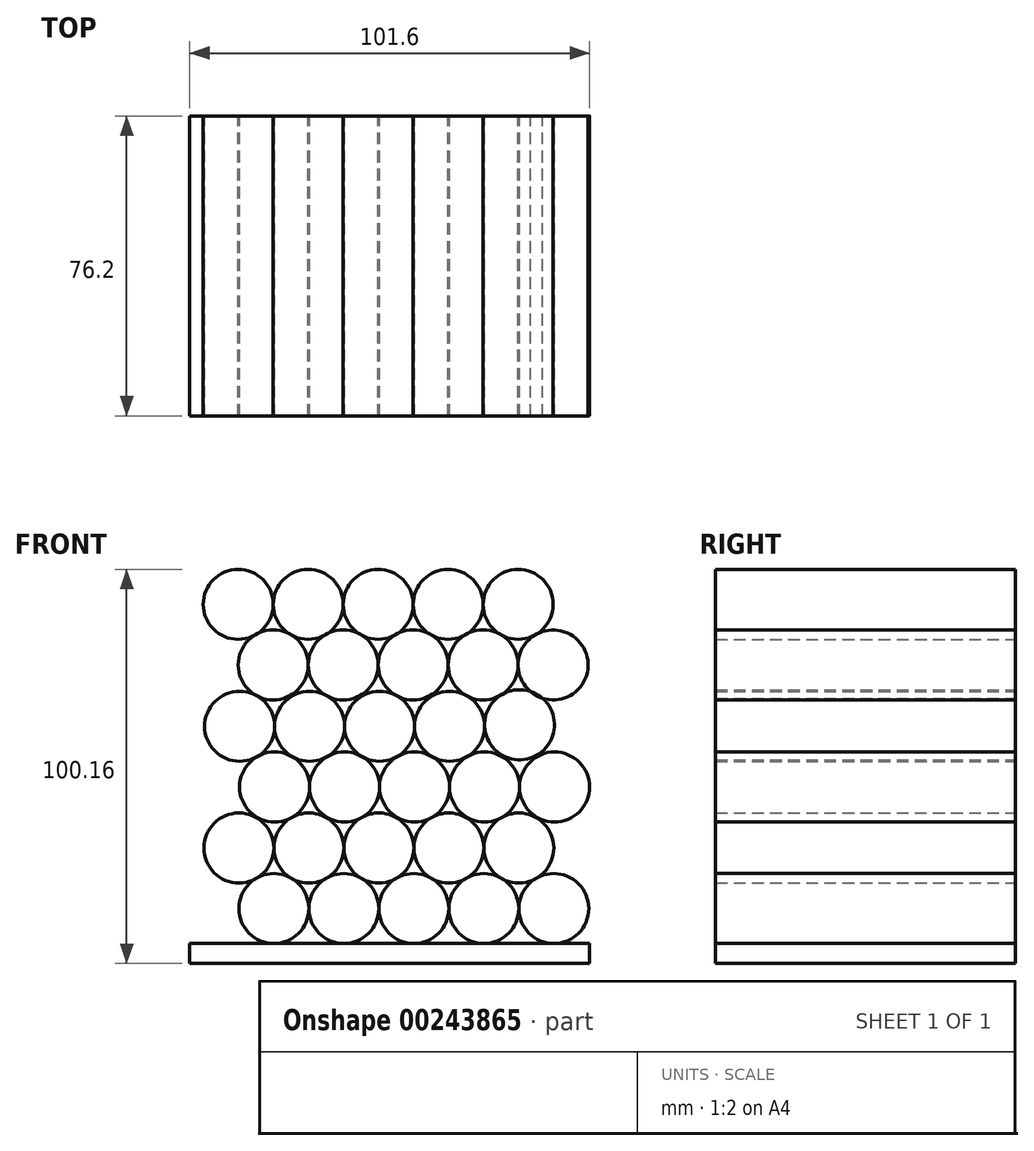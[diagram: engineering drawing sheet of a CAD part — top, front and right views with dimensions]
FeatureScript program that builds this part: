
annotation { "Feature Type Name" : "Feature", "Feature Type Description" : "" }
export const myFeature = defineFeature(function(context is Context, id is Id, definition is map)
    precondition{}
    {
        {
            var Q0;
            Q0=qCreatedBy(makeId("Front.planeOp"),FACE);
            var sketch = newSketch(context, id + "F0", { "sketchPlane" : qUnion([Q0])});
            skCircle(sketch, "E0", {"center": v(-29.45, -16.57) * mm, "radius": 8.9 * mm});
            skCircle(sketch, "E1", {"center": v(-11.67, -16.57) * mm, "radius": 8.9 * mm});
            skCircle(sketch, "E2", {"center": v(6.11, -16.57) * mm, "radius": 8.9 * mm});
            skCircle(sketch, "E3", {"center": v(23.9, -16.57) * mm, "radius": 8.9 * mm});
            skCircle(sketch, "E4", {"center": v(41.67, -16.57) * mm, "radius": 8.9 * mm});
            skLineSegment(sketch, "E5.bottom", {"start": v(-50.8, -25.46) * mm, "end": v(50.8, -25.46) * mm});
            skLineSegment(sketch, "E5.top", {"start": v(-50.8, -30.54) * mm, "end": v(50.8, -30.54) * mm});
            skLineSegment(sketch, "E5.left", {"start": v(-50.8, -25.46) * mm, "end": v(-50.8, -30.54) * mm});
            skLineSegment(sketch, "E5.right", {"start": v(50.8, -25.46) * mm, "end": v(50.8, -30.54) * mm});
            skCircle(sketch, "E6", {"center": v(-38.34, -1.17) * mm, "radius": 8.9 * mm});
            skCircle(sketch, "E7", {"center": v(-20.56, -1.17) * mm, "radius": 8.9 * mm});
            skCircle(sketch, "E8", {"center": v(-2.78, -1.17) * mm, "radius": 8.9 * mm});
            skCircle(sketch, "E9", {"center": v(15, -1.17) * mm, "radius": 8.9 * mm});
            skCircle(sketch, "E10", {"center": v(32.78, -1.17) * mm, "radius": 8.9 * mm});
            skCircle(sketch, "E11", {"center": v(-29.26, 14.34) * mm, "radius": 8.9 * mm});
            skCircle(sketch, "E12", {"center": v(-11.48, 14.34) * mm, "radius": 8.9 * mm});
            skCircle(sketch, "E13", {"center": v(6.3, 14.34) * mm, "radius": 8.9 * mm});
            skCircle(sketch, "E14", {"center": v(24.08, 14.34) * mm, "radius": 8.9 * mm});
            skCircle(sketch, "E15", {"center": v(41.86, 14.34) * mm, "radius": 8.9 * mm});
            skCircle(sketch, "E16", {"center": v(-38.15, 29.73) * mm, "radius": 8.9 * mm});
            skCircle(sketch, "E17", {"center": v(-20.37, 29.73) * mm, "radius": 8.9 * mm});
            skCircle(sketch, "E18", {"center": v(-2.6, 29.73) * mm, "radius": 8.9 * mm});
            skCircle(sketch, "E19", {"center": v(15.19, 29.73) * mm, "radius": 8.9 * mm});
            skCircle(sketch, "E20", {"center": v(32.96, 30.14) * mm, "radius": 8.9 * mm});
            skCircle(sketch, "E21", {"center": v(-29.62, 45.33) * mm, "radius": 8.9 * mm});
            skCircle(sketch, "E22", {"center": v(-11.84, 45.33) * mm, "radius": 8.9 * mm});
            skCircle(sketch, "E23", {"center": v(5.94, 45.33) * mm, "radius": 8.9 * mm});
            skCircle(sketch, "E24", {"center": v(23.72, 45.33) * mm, "radius": 8.9 * mm});
            skCircle(sketch, "E25", {"center": v(41.5, 45.33) * mm, "radius": 8.9 * mm});
            skCircle(sketch, "E26", {"center": v(-38.51, 60.73) * mm, "radius": 8.9 * mm});
            skCircle(sketch, "E27", {"center": v(-20.73, 60.73) * mm, "radius": 8.9 * mm});
            skCircle(sketch, "E28", {"center": v(-2.95, 60.73) * mm, "radius": 8.9 * mm});
            skCircle(sketch, "E29", {"center": v(14.83, 60.73) * mm, "radius": 8.9 * mm});
            skCircle(sketch, "E30", {"center": v(32.6, 60.73) * mm, "radius": 8.9 * mm});
            skSolve(sketch);
        }
        {
            var Q0;
            {var subQ0=sQuery(id+"F0.wireOp",EDGE,"0c1801c8-23d2-4a07-8585-4b4ae403161c");var subQ1=makeQuery(id+"F0.imprint","INTERSECT",VERTEX,{"derivedFrom":[sQuery(id+"F0.wireOp",EDGE,"f0896b75-7ff4-490b-9eb5-08945ea8ef80"),subQ0]});Q0=makeQuery(id+"F0.imprint","IMPRINT",FACE,{"disambiguationData":[TD([[makeQuery(id+"F0.imprint","IMPRINT",EDGE,{"disambiguationData":[TD([[subQ1,1.0]])],"derivedFrom":subQ0}),1.0]])]});}
            var Q1;
            {var subQ0=sQuery(id+"F0.wireOp",EDGE,"5af625b9-71d9-4944-9748-d1b5f725a47c");var subQ1=makeQuery(id+"F0.imprint","INTERSECT",VERTEX,{"derivedFrom":[sQuery(id+"F0.wireOp",EDGE,"0c1801c8-23d2-4a07-8585-4b4ae403161c"),subQ0]});Q1=makeQuery(id+"F0.imprint","IMPRINT",FACE,{"disambiguationData":[TD([[makeQuery(id+"F0.imprint","IMPRINT",EDGE,{"disambiguationData":[TD([[subQ1,1.0]])],"derivedFrom":subQ0}),1.0]])]});}
            var Q2;
            {var subQ0=sQuery(id+"F0.wireOp",EDGE,"cf587e86-f61d-495c-ab6c-7963b9340b9b");var subQ1=makeQuery(id+"F0.imprint","INTERSECT",VERTEX,{"derivedFrom":[sQuery(id+"F0.wireOp",EDGE,"5af625b9-71d9-4944-9748-d1b5f725a47c"),subQ0]});Q2=makeQuery(id+"F0.imprint","IMPRINT",FACE,{"disambiguationData":[TD([[makeQuery(id+"F0.imprint","IMPRINT",EDGE,{"disambiguationData":[TD([[subQ1,-1.0]])],"derivedFrom":subQ0}),1.0]])]});}
            var Q3;
            {var subQ0=sQuery(id+"F0.wireOp",EDGE,"6513f72b-f417-4675-a262-e46438cbcac2");var subQ1=makeQuery(id+"F0.imprint","INTERSECT",VERTEX,{"derivedFrom":[subQ0,sQuery(id+"F0.wireOp",EDGE,"cf587e86-f61d-495c-ab6c-7963b9340b9b")]});Q3=makeQuery(id+"F0.imprint","IMPRINT",FACE,{"disambiguationData":[TD([[makeQuery(id+"F0.imprint","IMPRINT",EDGE,{"disambiguationData":[TD([[subQ1,-1.0]])],"derivedFrom":subQ0}),1.0]])]});}
            var Q4;
            {var subQ0=sQuery(id+"F0.wireOp",EDGE,"b3fe10dc-f5bd-422b-85db-0323ad2a796b");var subQ4=makeQuery(id+"F0.imprint","INTERSECT",VERTEX,{"derivedFrom":[subQ0,sQuery(id+"F0.wireOp",EDGE,"cf587e86-f61d-495c-ab6c-7963b9340b9b")]});Q4=makeQuery(id+"F0.imprint","IMPRINT",FACE,{"disambiguationData":[TD([[makeQuery(id+"F0.imprint","IMPRINT",EDGE,{"disambiguationData":[TD([[subQ4,1.0]])],"derivedFrom":subQ0}),1.0]])]});}
            var Q5;
            {var subQ0=sQuery(id+"F0.wireOp",EDGE,"20095c58-7453-4e6b-84d0-4050fc440cec");var subQ4=makeQuery(id+"F0.imprint","INTERSECT",VERTEX,{"derivedFrom":[subQ0,sQuery(id+"F0.wireOp",EDGE,"5af625b9-71d9-4944-9748-d1b5f725a47c")]});Q5=makeQuery(id+"F0.imprint","IMPRINT",FACE,{"disambiguationData":[TD([[makeQuery(id+"F0.imprint","IMPRINT",EDGE,{"disambiguationData":[TD([[subQ4,1.0]])],"derivedFrom":subQ0}),1.0]])]});}
            var Q6;
            {var subQ0=sQuery(id+"F0.wireOp",EDGE,"f0896b75-7ff4-490b-9eb5-08945ea8ef80");var subQ1=makeQuery(id+"F0.imprint","INTERSECT",VERTEX,{"derivedFrom":[subQ0,sQuery(id+"F0.wireOp",EDGE,"0c1801c8-23d2-4a07-8585-4b4ae403161c")]});Q6=makeQuery(id+"F0.imprint","IMPRINT",FACE,{"disambiguationData":[TD([[makeQuery(id+"F0.imprint","IMPRINT",EDGE,{"disambiguationData":[TD([[subQ1,1.0]])],"derivedFrom":subQ0}),1.0]])]});}
            var Q7;
            {var subQ0=sQuery(id+"F0.wireOp",EDGE,"E0");var subQ1=makeQuery(id+"F0.imprint","INTERSECT",VERTEX,{"derivedFrom":[sQuery(id+"F0.wireOp",EDGE,"f0896b75-7ff4-490b-9eb5-08945ea8ef80"),subQ0]});Q7=makeQuery(id+"F0.imprint","IMPRINT",FACE,{"disambiguationData":[TD([[makeQuery(id+"F0.imprint","IMPRINT",EDGE,{"disambiguationData":[TD([[subQ1,1.0]])],"derivedFrom":subQ0}),1.0]])]});}
            var Q8;
            {var subQ0=sQuery(id+"F0.wireOp",EDGE,"E1");var subQ4=makeQuery(id+"F0.imprint","INTERSECT",VERTEX,{"derivedFrom":[sQuery(id+"F0.wireOp",EDGE,"20095c58-7453-4e6b-84d0-4050fc440cec"),subQ0]});Q8=makeQuery(id+"F0.imprint","IMPRINT",FACE,{"disambiguationData":[TD([[makeQuery(id+"F0.imprint","IMPRINT",EDGE,{"disambiguationData":[TD([[subQ4,1.0]])],"derivedFrom":subQ0}),1.0]])]});}
            var Q9;
            {var subQ0=sQuery(id+"F0.wireOp",EDGE,"E2");var subQ4=makeQuery(id+"F0.imprint","INTERSECT",VERTEX,{"derivedFrom":[sQuery(id+"F0.wireOp",EDGE,"b3fe10dc-f5bd-422b-85db-0323ad2a796b"),subQ0]});Q9=makeQuery(id+"F0.imprint","IMPRINT",FACE,{"disambiguationData":[TD([[makeQuery(id+"F0.imprint","IMPRINT",EDGE,{"disambiguationData":[TD([[subQ4,1.0]])],"derivedFrom":subQ0}),1.0]])]});}
            var Q10;
            {var subQ0=sQuery(id+"F0.wireOp",EDGE,"E3");var subQ4=makeQuery(id+"F0.imprint","INTERSECT",VERTEX,{"derivedFrom":[sQuery(id+"F0.wireOp",EDGE,"6513f72b-f417-4675-a262-e46438cbcac2"),subQ0]});Q10=makeQuery(id+"F0.imprint","IMPRINT",FACE,{"disambiguationData":[TD([[makeQuery(id+"F0.imprint","IMPRINT",EDGE,{"disambiguationData":[TD([[subQ4,1.0]])],"derivedFrom":subQ0}),1.0]])]});}
            var Q11;
            {var subQ0=sQuery(id+"F0.wireOp",EDGE,"E4");var subQ1=makeQuery(id+"F0.imprint","INTERSECT",VERTEX,{"derivedFrom":[sQuery(id+"F0.wireOp",EDGE,"6513f72b-f417-4675-a262-e46438cbcac2"),subQ0]});Q11=makeQuery(id+"F0.imprint","IMPRINT",FACE,{"disambiguationData":[TD([[makeQuery(id+"F0.imprint","IMPRINT",EDGE,{"disambiguationData":[TD([[subQ1,-1.0]])],"derivedFrom":subQ0}),1.0]])]});}
            var Q12;
            Q12=makeQuery(id+"F0.imprint","IMPRINT",FACE,{"disambiguationData":[TD([[makeQuery(id+"F0.imprint","IMPRINT",EDGE,{"derivedFrom":sQuery(id+"F0.wireOp",EDGE,"E5.top")}),1.0]])]});
            var Q13;
            {var subQ0=sQuery(id+"F0.wireOp",EDGE,"b7209964-fce2-4c74-a03b-dcfcf9720273");var subQ1=makeQuery(id+"F0.imprint","INTERSECT",VERTEX,{"derivedFrom":[subQ0,sQuery(id+"F0.wireOp",EDGE,"826bc404-7e04-4ebb-a8bb-261f92a73414")]});Q13=makeQuery(id+"F0.imprint","IMPRINT",FACE,{"disambiguationData":[TD([[makeQuery(id+"F0.imprint","IMPRINT",EDGE,{"disambiguationData":[TD([[subQ1,1.0]])],"derivedFrom":subQ0}),1.0]])]});}
            var Q14;
            {var subQ0=sQuery(id+"F0.wireOp",EDGE,"4bfdec23-dac0-4773-80be-c3509125d457");var subQ1=makeQuery(id+"F0.imprint","INTERSECT",VERTEX,{"derivedFrom":[subQ0,sQuery(id+"F0.wireOp",EDGE,"826bc404-7e04-4ebb-a8bb-261f92a73414")]});Q14=makeQuery(id+"F0.imprint","IMPRINT",FACE,{"disambiguationData":[TD([[makeQuery(id+"F0.imprint","IMPRINT",EDGE,{"disambiguationData":[TD([[subQ1,-1.0]])],"derivedFrom":subQ0}),1.0]])]});}
            var Q15;
            {var subQ0=sQuery(id+"F0.wireOp",EDGE,"826bc404-7e04-4ebb-a8bb-261f92a73414");var subQ1=makeQuery(id+"F0.imprint","INTERSECT",VERTEX,{"derivedFrom":[sQuery(id+"F0.wireOp",EDGE,"b7209964-fce2-4c74-a03b-dcfcf9720273"),subQ0]});Q15=makeQuery(id+"F0.imprint","IMPRINT",FACE,{"disambiguationData":[TD([[makeQuery(id+"F0.imprint","IMPRINT",EDGE,{"disambiguationData":[TD([[subQ1,-1.0]])],"derivedFrom":subQ0}),1.0]])]});}
            var Q16;
            {var subQ0=sQuery(id+"F0.wireOp",EDGE,"E6");var subQ1=makeQuery(id+"F0.imprint","INTERSECT",VERTEX,{"derivedFrom":[sQuery(id+"F0.wireOp",EDGE,"E0"),subQ0]});Q16=makeQuery(id+"F0.imprint","IMPRINT",FACE,{"disambiguationData":[TD([[makeQuery(id+"F0.imprint","IMPRINT",EDGE,{"disambiguationData":[TD([[subQ1,1.0]])],"derivedFrom":subQ0}),1.0]])]});}
            var Q17;
            {var subQ0=sQuery(id+"F0.wireOp",EDGE,"E7");var subQ4=makeQuery(id+"F0.imprint","INTERSECT",VERTEX,{"derivedFrom":[subQ0,sQuery(id+"F0.wireOp",EDGE,"E11")]});Q17=makeQuery(id+"F0.imprint","IMPRINT",FACE,{"disambiguationData":[TD([[makeQuery(id+"F0.imprint","IMPRINT",EDGE,{"disambiguationData":[TD([[subQ4,1.0]])],"derivedFrom":subQ0}),1.0]])]});}
            var Q18;
            {var subQ0=sQuery(id+"F0.wireOp",EDGE,"E8");var subQ4=makeQuery(id+"F0.imprint","INTERSECT",VERTEX,{"derivedFrom":[subQ0,sQuery(id+"F0.wireOp",EDGE,"E12")]});Q18=makeQuery(id+"F0.imprint","IMPRINT",FACE,{"disambiguationData":[TD([[makeQuery(id+"F0.imprint","IMPRINT",EDGE,{"disambiguationData":[TD([[subQ4,1.0]])],"derivedFrom":subQ0}),1.0]])]});}
            var Q19;
            {var subQ0=sQuery(id+"F0.wireOp",EDGE,"E9");var subQ4=makeQuery(id+"F0.imprint","INTERSECT",VERTEX,{"derivedFrom":[subQ0,sQuery(id+"F0.wireOp",EDGE,"E13")]});Q19=makeQuery(id+"F0.imprint","IMPRINT",FACE,{"disambiguationData":[TD([[makeQuery(id+"F0.imprint","IMPRINT",EDGE,{"disambiguationData":[TD([[subQ4,1.0]])],"derivedFrom":subQ0}),1.0]])]});}
            var Q20;
            {var subQ0=sQuery(id+"F0.wireOp",EDGE,"E10");var subQ1=makeQuery(id+"F0.imprint","INTERSECT",VERTEX,{"derivedFrom":[subQ0,sQuery(id+"F0.wireOp",EDGE,"E14")]});Q20=makeQuery(id+"F0.imprint","IMPRINT",FACE,{"disambiguationData":[TD([[makeQuery(id+"F0.imprint","IMPRINT",EDGE,{"disambiguationData":[TD([[subQ1,-1.0]])],"derivedFrom":subQ0}),1.0]])]});}
            var Q21;
            {var subQ0=sQuery(id+"F0.wireOp",EDGE,"E15");var subQ1=makeQuery(id+"F0.imprint","INTERSECT",VERTEX,{"derivedFrom":[sQuery(id+"F0.wireOp",EDGE,"E14"),subQ0]});Q21=makeQuery(id+"F0.imprint","IMPRINT",FACE,{"disambiguationData":[TD([[makeQuery(id+"F0.imprint","IMPRINT",EDGE,{"disambiguationData":[TD([[subQ1,1.0]])],"derivedFrom":subQ0}),1.0]])]});}
            var Q22;
            {var subQ0=sQuery(id+"F0.wireOp",EDGE,"E14");var subQ5=makeQuery(id+"F0.imprint","INTERSECT",VERTEX,{"derivedFrom":[subQ0,sQuery(id+"F0.wireOp",EDGE,"E15")]});Q22=makeQuery(id+"F0.imprint","IMPRINT",FACE,{"disambiguationData":[TD([[makeQuery(id+"F0.imprint","IMPRINT",EDGE,{"disambiguationData":[TD([[subQ5,-1.0]])],"derivedFrom":subQ0}),1.0]])]});}
            var Q23;
            {var subQ0=sQuery(id+"F0.wireOp",EDGE,"E13");var subQ4=makeQuery(id+"F0.imprint","INTERSECT",VERTEX,{"derivedFrom":[subQ0,sQuery(id+"F0.wireOp",EDGE,"E19")]});Q23=makeQuery(id+"F0.imprint","IMPRINT",FACE,{"disambiguationData":[TD([[makeQuery(id+"F0.imprint","IMPRINT",EDGE,{"disambiguationData":[TD([[subQ4,1.0]])],"derivedFrom":subQ0}),1.0]])]});}
            var Q24;
            {var subQ0=sQuery(id+"F0.wireOp",EDGE,"E12");var subQ4=makeQuery(id+"F0.imprint","INTERSECT",VERTEX,{"derivedFrom":[subQ0,sQuery(id+"F0.wireOp",EDGE,"E18")]});Q24=makeQuery(id+"F0.imprint","IMPRINT",FACE,{"disambiguationData":[TD([[makeQuery(id+"F0.imprint","IMPRINT",EDGE,{"disambiguationData":[TD([[subQ4,1.0]])],"derivedFrom":subQ0}),1.0]])]});}
            var Q25;
            {var subQ0=sQuery(id+"F0.wireOp",EDGE,"E11");var subQ1=makeQuery(id+"F0.imprint","INTERSECT",VERTEX,{"derivedFrom":[subQ0,sQuery(id+"F0.wireOp",EDGE,"E17")]});Q25=makeQuery(id+"F0.imprint","IMPRINT",FACE,{"disambiguationData":[TD([[makeQuery(id+"F0.imprint","IMPRINT",EDGE,{"disambiguationData":[TD([[subQ1,1.0]])],"derivedFrom":subQ0}),1.0]])]});}
            var Q26;
            {var subQ0=sQuery(id+"F0.wireOp",EDGE,"E16");var subQ1=makeQuery(id+"F0.imprint","INTERSECT",VERTEX,{"derivedFrom":[sQuery(id+"F0.wireOp",EDGE,"E11"),subQ0]});Q26=makeQuery(id+"F0.imprint","IMPRINT",FACE,{"disambiguationData":[TD([[makeQuery(id+"F0.imprint","IMPRINT",EDGE,{"disambiguationData":[TD([[subQ1,1.0]])],"derivedFrom":subQ0}),1.0]])]});}
            var Q27;
            {var subQ0=sQuery(id+"F0.wireOp",EDGE,"E17");var subQ1=makeQuery(id+"F0.imprint","INTERSECT",VERTEX,{"derivedFrom":[sQuery(id+"F0.wireOp",EDGE,"E16"),subQ0]});Q27=makeQuery(id+"F0.imprint","IMPRINT",FACE,{"disambiguationData":[TD([[makeQuery(id+"F0.imprint","IMPRINT",EDGE,{"disambiguationData":[TD([[subQ1,1.0]])],"derivedFrom":subQ0}),1.0]])]});}
            var Q28;
            {var subQ0=sQuery(id+"F0.wireOp",EDGE,"E18");var subQ1=makeQuery(id+"F0.imprint","INTERSECT",VERTEX,{"derivedFrom":[sQuery(id+"F0.wireOp",EDGE,"E17"),subQ0]});Q28=makeQuery(id+"F0.imprint","IMPRINT",FACE,{"disambiguationData":[TD([[makeQuery(id+"F0.imprint","IMPRINT",EDGE,{"disambiguationData":[TD([[subQ1,1.0]])],"derivedFrom":subQ0}),1.0]])]});}
            var Q29;
            {var subQ0=sQuery(id+"F0.wireOp",EDGE,"E19");var subQ1=makeQuery(id+"F0.imprint","INTERSECT",VERTEX,{"derivedFrom":[sQuery(id+"F0.wireOp",EDGE,"E18"),subQ0]});Q29=makeQuery(id+"F0.imprint","IMPRINT",FACE,{"disambiguationData":[TD([[makeQuery(id+"F0.imprint","IMPRINT",EDGE,{"disambiguationData":[TD([[subQ1,1.0]])],"derivedFrom":subQ0}),1.0]])]});}
            var Q30;
            {var subQ0=sQuery(id+"F0.wireOp",EDGE,"E20");var subQ1=makeQuery(id+"F0.imprint","INTERSECT",VERTEX,{"derivedFrom":[sQuery(id+"F0.wireOp",EDGE,"E19"),subQ0]});Q30=makeQuery(id+"F0.imprint","IMPRINT",FACE,{"disambiguationData":[TD([[makeQuery(id+"F0.imprint","IMPRINT",EDGE,{"disambiguationData":[TD([[subQ1,-1.0]])],"derivedFrom":subQ0}),1.0]])]});}
            var Q31;
            {var subQ0=sQuery(id+"F0.wireOp",EDGE,"E21");var subQ1=makeQuery(id+"F0.imprint","INTERSECT",VERTEX,{"derivedFrom":[subQ0,sQuery(id+"F0.wireOp",EDGE,"E27")]});Q31=makeQuery(id+"F0.imprint","IMPRINT",FACE,{"disambiguationData":[TD([[makeQuery(id+"F0.imprint","IMPRINT",EDGE,{"disambiguationData":[TD([[subQ1,1.0]])],"derivedFrom":subQ0}),1.0]])]});}
            var Q32;
            {var subQ0=sQuery(id+"F0.wireOp",EDGE,"E22");var subQ4=makeQuery(id+"F0.imprint","INTERSECT",VERTEX,{"derivedFrom":[subQ0,sQuery(id+"F0.wireOp",EDGE,"E28")]});Q32=makeQuery(id+"F0.imprint","IMPRINT",FACE,{"disambiguationData":[TD([[makeQuery(id+"F0.imprint","IMPRINT",EDGE,{"disambiguationData":[TD([[subQ4,1.0]])],"derivedFrom":subQ0}),1.0]])]});}
            var Q33;
            {var subQ0=sQuery(id+"F0.wireOp",EDGE,"E23");var subQ4=makeQuery(id+"F0.imprint","INTERSECT",VERTEX,{"derivedFrom":[subQ0,sQuery(id+"F0.wireOp",EDGE,"E29")]});Q33=makeQuery(id+"F0.imprint","IMPRINT",FACE,{"disambiguationData":[TD([[makeQuery(id+"F0.imprint","IMPRINT",EDGE,{"disambiguationData":[TD([[subQ4,1.0]])],"derivedFrom":subQ0}),1.0]])]});}
            var Q34;
            {var subQ0=sQuery(id+"F0.wireOp",EDGE,"E24");var subQ4=makeQuery(id+"F0.imprint","INTERSECT",VERTEX,{"derivedFrom":[subQ0,sQuery(id+"F0.wireOp",EDGE,"E30")]});Q34=makeQuery(id+"F0.imprint","IMPRINT",FACE,{"disambiguationData":[TD([[makeQuery(id+"F0.imprint","IMPRINT",EDGE,{"disambiguationData":[TD([[subQ4,1.0]])],"derivedFrom":subQ0}),1.0]])]});}
            var Q35;
            {var subQ0=sQuery(id+"F0.wireOp",EDGE,"E25");var subQ1=sQuery(id+"F0.wireOp",EDGE,"E20");var subQ2=makeQuery(id+"F0.imprint","INTERSECT",VERTEX,{"disambiguationData":[OD(0.0)],"derivedFrom":[subQ1,subQ0]});Q35=makeQuery(id+"F0.imprint","IMPRINT",FACE,{"disambiguationData":[TD([[makeQuery(id+"F0.imprint","IMPRINT",EDGE,{"disambiguationData":[TD([[subQ2,-1.0]])],"derivedFrom":subQ1}),-1.0]])]});}
            var Q36;
            {var subQ0=sQuery(id+"F0.wireOp",EDGE,"E30");var subQ1=makeQuery(id+"F0.imprint","INTERSECT",VERTEX,{"derivedFrom":[sQuery(id+"F0.wireOp",EDGE,"E29"),subQ0]});Q36=makeQuery(id+"F0.imprint","IMPRINT",FACE,{"disambiguationData":[TD([[makeQuery(id+"F0.imprint","IMPRINT",EDGE,{"disambiguationData":[TD([[subQ1,-1.0]])],"derivedFrom":subQ0}),1.0]])]});}
            var Q37;
            {var subQ0=sQuery(id+"F0.wireOp",EDGE,"E29");var subQ1=makeQuery(id+"F0.imprint","INTERSECT",VERTEX,{"derivedFrom":[sQuery(id+"F0.wireOp",EDGE,"E28"),subQ0]});Q37=makeQuery(id+"F0.imprint","IMPRINT",FACE,{"disambiguationData":[TD([[makeQuery(id+"F0.imprint","IMPRINT",EDGE,{"disambiguationData":[TD([[subQ1,1.0]])],"derivedFrom":subQ0}),1.0]])]});}
            var Q38;
            {var subQ0=sQuery(id+"F0.wireOp",EDGE,"E28");var subQ1=makeQuery(id+"F0.imprint","INTERSECT",VERTEX,{"derivedFrom":[sQuery(id+"F0.wireOp",EDGE,"E27"),subQ0]});Q38=makeQuery(id+"F0.imprint","IMPRINT",FACE,{"disambiguationData":[TD([[makeQuery(id+"F0.imprint","IMPRINT",EDGE,{"disambiguationData":[TD([[subQ1,1.0]])],"derivedFrom":subQ0}),1.0]])]});}
            var Q39;
            {var subQ0=sQuery(id+"F0.wireOp",EDGE,"E27");var subQ1=makeQuery(id+"F0.imprint","INTERSECT",VERTEX,{"derivedFrom":[sQuery(id+"F0.wireOp",EDGE,"E26"),subQ0]});Q39=makeQuery(id+"F0.imprint","IMPRINT",FACE,{"disambiguationData":[TD([[makeQuery(id+"F0.imprint","IMPRINT",EDGE,{"disambiguationData":[TD([[subQ1,1.0]])],"derivedFrom":subQ0}),1.0]])]});}
            var Q40;
            {var subQ0=sQuery(id+"F0.wireOp",EDGE,"E26");var subQ1=makeQuery(id+"F0.imprint","INTERSECT",VERTEX,{"derivedFrom":[sQuery(id+"F0.wireOp",EDGE,"E21"),subQ0]});Q40=makeQuery(id+"F0.imprint","IMPRINT",FACE,{"disambiguationData":[TD([[makeQuery(id+"F0.imprint","IMPRINT",EDGE,{"disambiguationData":[TD([[subQ1,1.0]])],"derivedFrom":subQ0}),1.0]])]});}
            var Q41;
            Q41=sQuery(id+"F0.wireOp",EDGE,"5af625b9-71d9-4944-9748-d1b5f725a47c");
            var Q42;
            Q42=sQuery(id+"F0.wireOp",EDGE,"cf587e86-f61d-495c-ab6c-7963b9340b9b");
            var Q43;
            Q43=sQuery(id+"F0.wireOp",EDGE,"E5.bottom");
            var Q44;
            Q44=sQuery(id+"F0.wireOp",EDGE,"20095c58-7453-4e6b-84d0-4050fc440cec");
            var Q45;
            Q45=sQuery(id+"F0.wireOp",EDGE,"6513f72b-f417-4675-a262-e46438cbcac2");
            var Q46;
            Q46=sQuery(id+"F0.wireOp",EDGE,"0c1801c8-23d2-4a07-8585-4b4ae403161c");
            var Q47;
            Q47=sQuery(id+"F0.wireOp",EDGE,"E4");
            var Q48;
            Q48=sQuery(id+"F0.wireOp",EDGE,"E1");
            var Q49;
            Q49=sQuery(id+"F0.wireOp",EDGE,"b3fe10dc-f5bd-422b-85db-0323ad2a796b");
            var Q50;
            Q50=sQuery(id+"F0.wireOp",EDGE,"E5.top");
            var Q51;
            Q51=sQuery(id+"F0.wireOp",EDGE,"f0896b75-7ff4-490b-9eb5-08945ea8ef80");
            var Q52;
            Q52=sQuery(id+"F0.wireOp",EDGE,"E2");
            var Q53;
            Q53=sQuery(id+"F0.wireOp",EDGE,"E3");
            var Q54;
            Q54=sQuery(id+"F0.wireOp",EDGE,"E0");
            var Q55;
            Q55=sQuery(id+"F0.wireOp",EDGE,"E5.left");
            var Q56;
            Q56=sQuery(id+"F0.wireOp",EDGE,"E5.right");
            extrude(context, id + "F1", {"entities" : qUnion([Q0, Q1, Q2, Q3, Q4, Q5, Q6, Q7, Q8, Q9, Q10, Q11, Q12, Q13, Q14, Q15, Q16, Q17, Q18, Q19, Q20, Q21, Q22, Q23, Q24, Q25, Q26, Q27, Q28, Q29, Q30, Q31, Q32, Q33, Q34, Q35, Q36, Q37, Q38, Q39, Q40]), "surfaceEntities" : qUnion([Q41, Q42, Q43, Q44, Q45, Q46, Q47, Q48, Q49, Q50, Q51, Q52, Q53, Q54, Q55, Q56]), "depth" : 76.2 * mm});
        }
    });
